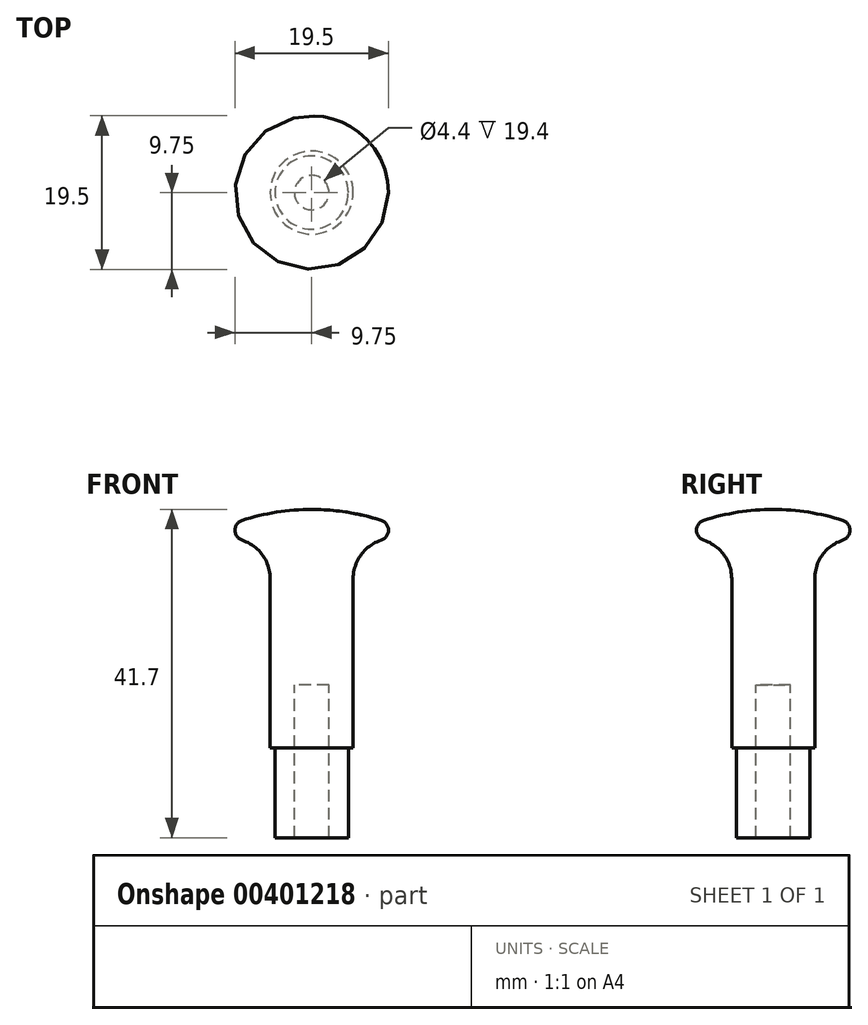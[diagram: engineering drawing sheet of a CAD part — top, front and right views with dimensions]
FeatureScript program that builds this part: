
annotation { "Feature Type Name" : "Feature", "Feature Type Description" : "" }
export const myFeature = defineFeature(function(context is Context, id is Id, definition is map)
    precondition{}
    {
        {
            var Q0;
            Q0=qCreatedBy(makeId("Front.planeOp"),FACE);
            var sketch = newSketch(context, id + "F0", { "sketchPlane" : qUnion([Q0])});
            skLineSegment(sketch, "E0", {"start": v(0, 8) * mm, "end": v(-2.2, 8) * mm});
            skLineSegment(sketch, "E1", {"start": v(-2.2, 8) * mm, "end": v(-2.2, -11.4) * mm});
            skLineSegment(sketch, "E2", {"start": v(-4.65, 0) * mm, "end": v(-5.27, 0) * mm});
            skLineSegment(sketch, "E3", {"start": v(-5.27, 0) * mm, "end": v(-5.27, 21.48) * mm});
            skLineSegment(sketch, "E4", {"start": v(0, 30.3) * mm, "end": v(0, 8) * mm});
            skArc(sketch, "E5", {"start": v(0, 30.3) * mm, "mid": v(-4.48, 29.95) * mm, "end": v(-8.84, 28.9) * mm});
            skArc(sketch, "E6", {"start": v(-8.84, 28.9) * mm, "mid": v(-9.75, 27.65) * mm, "end": v(-8.84, 26.4) * mm});
            skArc(sketch, "E7", {"start": v(-8.84, 26.4) * mm, "mid": v(-6.26, 24.52) * mm, "end": v(-5.27, 21.48) * mm});
            skLineSegment(sketch, "E8", {"start": v(-4.65, 0) * mm, "end": v(-4.65, -11.4) * mm});
            skLineSegment(sketch, "E9", {"start": v(-4.65, -11.4) * mm, "end": v(-2.2, -11.4) * mm});
            skSolve(sketch);
        }
        {
            var Q0;
            Q0=makeQuery(id+"F0.imprint","IMPRINT",FACE,{"disambiguationData":[TD([[makeQuery(id+"F0.imprint","IMPRINT",EDGE,{"derivedFrom":sQuery(id+"F0.wireOp",EDGE,"E0")}),-1.0]])]});
            var Q1;
            Q1=sQuery(id+"F0.wireOp",EDGE,"E4");
            revolve(context, id + "F1", {"surfaceOperationType" : NewSurfaceOperationType.NEW, "entities" : qUnion([Q0]), "axis" : qUnion([Q1]), "revolveType" : RevolveType.FULL});
        }
    });
